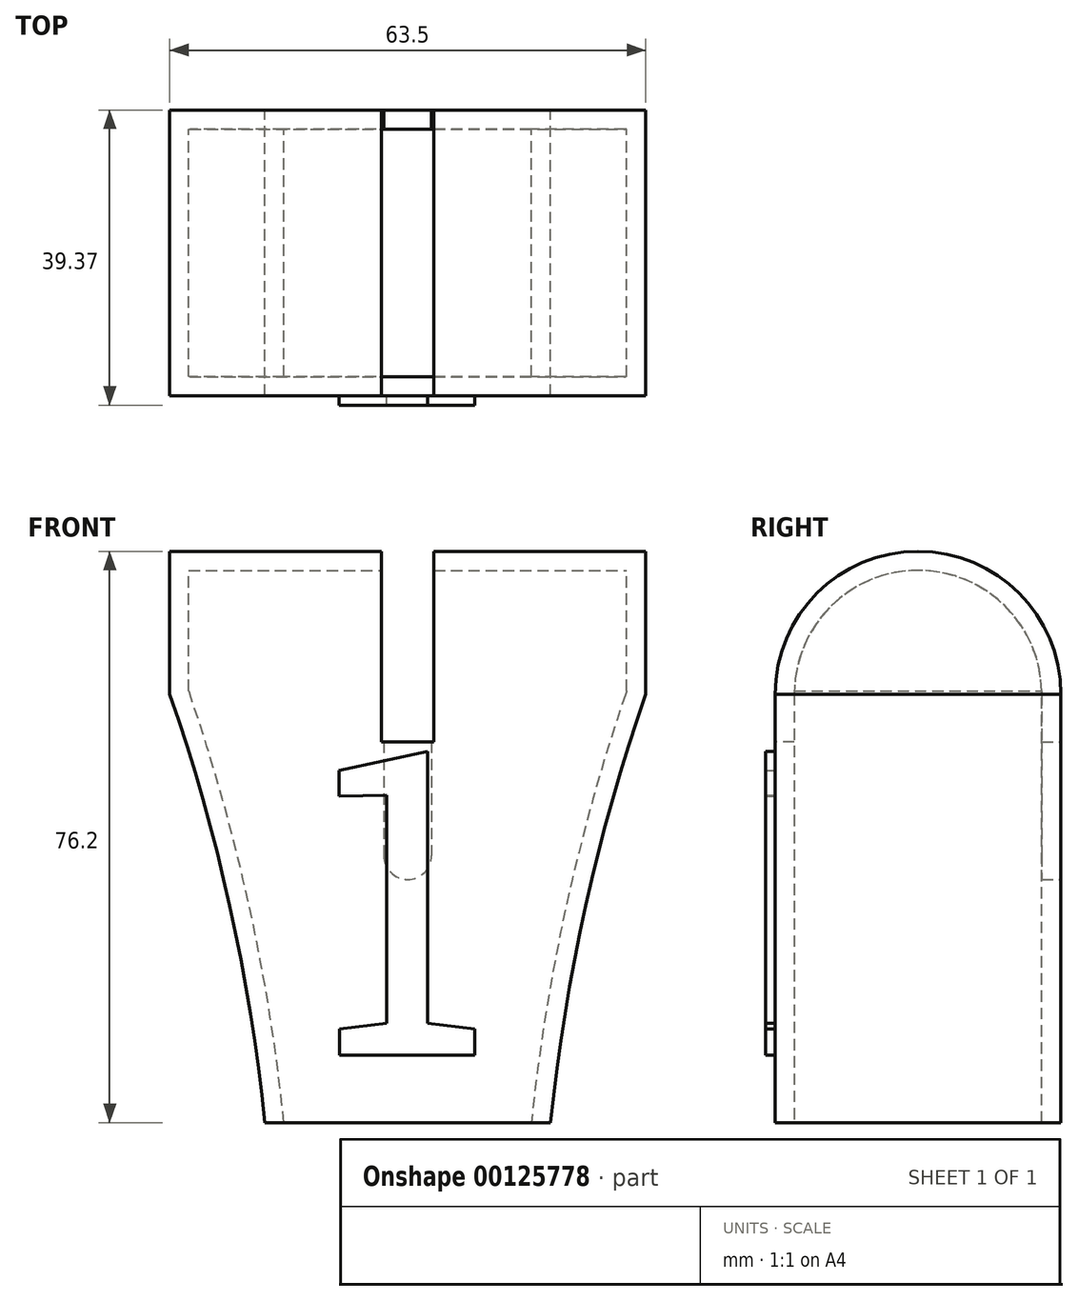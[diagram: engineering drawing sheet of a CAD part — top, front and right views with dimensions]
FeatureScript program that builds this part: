
annotation { "Feature Type Name" : "Feature", "Feature Type Description" : "" }
export const myFeature = defineFeature(function(context is Context, id is Id, definition is map)
    precondition{}
    {
        {
            var Q0;
            Q0=qCreatedBy(makeId("Front.planeOp"),FACE);
            var sketch = newSketch(context, id + "F0", { "sketchPlane" : qUnion([Q0])});
            skLineSegment(sketch, "E0.bottom", {"start": v(19.05, -38.1) * mm, "end": v(-19.05, -38.1) * mm});
            skLineSegment(sketch, "E0.top", {"start": v(31.75, 38.1) * mm, "end": v(-31.75, 38.1) * mm});
            skLineSegment(sketch, "E0.left", {"start": v(31.75, 19.05) * mm, "end": v(31.75, 38.1) * mm});
            skLineSegment(sketch, "E0.right", {"start": v(-31.75, 19.05) * mm, "end": v(-31.75, 38.1) * mm});
            skPoint(sketch, "E0.middle", {"position": v(0, 0) * mm});
            skPoint(sketch, "E1", {"position": v(31.75, 19.05) * mm});
            skPoint(sketch, "E2", {"position": v(-31.75, 19.05) * mm});
            skArc(sketch, "E3", {"start": v(31.75, 19.05) * mm, "mid": v(23.75, -9.16) * mm, "end": v(19.05, -38.1) * mm});
            skArc(sketch, "E4", {"start": v(-19.05, -38.1) * mm, "mid": v(-23.75, -9.16) * mm, "end": v(-31.75, 19.05) * mm});
            skPoint(sketch, "E5.orphan", {"position": v(31.75, -38.1) * mm});
            skPoint(sketch, "E6.orphan", {"position": v(-31.75, -38.1) * mm});
            skSolve(sketch);
        }
        {
            var Q0;
            Q0=qSketchRegion(id+"F0",true);
            extrude(context, id + "F1", {"entities" : qUnion([Q0]), "endBound" : BoundingType.SYMMETRIC, "depth" : 38.1 * mm});
        }
        {
            var Q0;
            Q0=qCreatedBy(makeId("Right.planeOp"),FACE);
            var sketch = newSketch(context, id + "F2", { "sketchPlane" : qUnion([Q0])});
            skArc(sketch, "E7", {"start": v(19.05, 19.05) * mm, "mid": v(0, 38.1) * mm, "end": v(-19.05, 19.05) * mm});
            skLineSegment(sketch, "E8", {"start": v(19.05, 19.05) * mm, "end": v(44.45, 19.05) * mm});
            skLineSegment(sketch, "E9", {"start": v(-19.05, 19.05) * mm, "end": v(-44.45, 19.05) * mm});
            skLineSegment(sketch, "E10", {"start": v(-44.45, 19.05) * mm, "end": v(-44.45, 44.45) * mm});
            skLineSegment(sketch, "E11", {"start": v(-44.45, 44.45) * mm, "end": v(44.45, 44.45) * mm});
            skLineSegment(sketch, "E12", {"start": v(44.45, 44.45) * mm, "end": v(44.45, 19.05) * mm});
            skPoint(sketch, "E13", {"position": v(0, 38.1) * mm});
            skSolve(sketch);
        }
        {
            var Q0;
            Q0=qSketchRegion(id+"F2",true);
            extrude(context, id + "F3", {"entities" : qUnion([Q0]), "operationType" : NewBodyOperationType.REMOVE, "endBound" : BoundingType.SYMMETRIC, "oppositeDirection" : true, "depth" : 127 * mm});
        }
        {
            var Q0;
            Q0=makeQuery(id+"F1.opExtrude","CAP_FACE",FACE,{"disambiguationData":[OSD([sQuery(id+"F0.wireOp",EDGE,"E0.bottom"),sQuery(id+"F0.wireOp",EDGE,"E0.top"),sQuery(id+"F0.wireOp",EDGE,"E0.left"),sQuery(id+"F0.wireOp",EDGE,"E0.right"),sQuery(id+"F0.wireOp",EDGE,"E3"),sQuery(id+"F0.wireOp",EDGE,"E4")])],"isStart":true});
            var sketch = newSketch(context, id + "F4", { "sketchPlane" : qUnion([Q0])});
            skLineSegment(sketch, "E14.bottom", {"start": v(3.17, -2.5) * mm, "end": v(-3.18, -2.5) * mm});
            skLineSegment(sketch, "E14.top", {"start": v(3.17, 29.26) * mm, "end": v(-3.18, 29.26) * mm});
            skLineSegment(sketch, "E14.left", {"start": v(3.17, -2.5) * mm, "end": v(3.17, 29.26) * mm});
            skLineSegment(sketch, "E14.right", {"start": v(-3.18, -2.5) * mm, "end": v(-3.18, 29.26) * mm});
            skPoint(sketch, "E14.middle", {"position": v(0, 13.38) * mm});
            skArc(sketch, "E15", {"start": v(3.17, 29.26) * mm, "mid": v(0, 32.43) * mm, "end": v(-3.18, 29.26) * mm});
            skLineSegment(sketch, "E16", {"start": v(-3.18, 13.38) * mm, "end": v(3.17, 13.38) * mm, "construction": true});
            skArc(sketch, "E17.MirrorCS", {"start": v(3.17, -2.5) * mm, "mid": v(0, -5.67) * mm, "end": v(-3.18, -2.5) * mm});
            skSolve(sketch);
        }
        {
            var Q0;
            Q0=makeQuery(id+"F1.opExtrude","SWEPT_FACE",FACE,{"disambiguationData":[OSD([sQuery(id+"F0.wireOp",EDGE,"E0.bottom")])]});
            shell(context, id + "F5", {"entities" : qUnion([Q0]), "thickness" : 2.54 * mm});
        }
        {
            var Q0;
            Q0=qSketchRegion(id+"F4",true);
            extrude(context, id + "F6", {"entities" : qUnion([Q0]), "operationType" : NewBodyOperationType.REMOVE, "oppositeDirection" : true, "depth" : 4.48 * mm});
        }
        {
            var Q0;
            Q0=qCreatedBy(makeId("Top.planeOp"),FACE);
            var Q1;
            Q1=sQuery(id+"F2.wireOp",VERTEX,"E13");
            cPlane(context, id + "F7", {"entities" : qUnion([Q0, Q1]), "cplaneType" : CPlaneType.PLANE_POINT, "offset" : 25.4 * mm, "width" : 152.4 * mm, "height" : 152.4 * mm});
        }
        {
            var Q0;
            Q0=qCreatedBy(id+"F7.planeOp",FACE);
            var sketch = newSketch(context, id + "F8", { "sketchPlane" : qUnion([Q0])});
            skLineSegment(sketch, "E18.bottom", {"start": v(-3.5, 19.05) * mm, "end": v(3.5, 19.05) * mm});
            skLineSegment(sketch, "E18.left", {"start": v(-3.5, 19.05) * mm, "end": v(-3.5, -19.05) * mm});
            skLineSegment(sketch, "E18.right", {"start": v(3.5, 19.05) * mm, "end": v(3.5, -19.05) * mm});
            skPoint(sketch, "E19", {"position": v(0, 0) * mm});
            skLineSegment(sketch, "E20", {"start": v(3.5, 0) * mm, "end": v(-3.5, 0) * mm, "construction": true});
            skLineSegment(sketch, "E21", {"start": v(-3.5, -19.05) * mm, "end": v(3.5, -19.05) * mm});
            skSolve(sketch);
        }
        {
            var Q0;
            Q0=qSketchRegion(id+"F8",true);
            extrude(context, id + "F9", {"entities" : qUnion([Q0]), "operationType" : NewBodyOperationType.REMOVE, "oppositeDirection" : true, "depth" : 25.4 * mm});
        }
        {
            var Q0;
            Q0=makeQuery(id+"F1.opExtrude","CAP_FACE",FACE,{"disambiguationData":[OSD([sQuery(id+"F0.wireOp",EDGE,"E0.bottom"),sQuery(id+"F0.wireOp",EDGE,"E0.top"),sQuery(id+"F0.wireOp",EDGE,"E0.left"),sQuery(id+"F0.wireOp",EDGE,"E0.right"),sQuery(id+"F0.wireOp",EDGE,"E3"),sQuery(id+"F0.wireOp",EDGE,"E4")])],"isStart":false});
            var sketch = newSketch(context, id + "F10", { "sketchPlane" : qUnion([Q0])});
            skText(sketch, "E22", { "text": "1", "fontName": "RobotoSlab-Regular.ttf"});
            const initialGuessF10  = {"E22": [-0.01245, -0.02912, 1, 0, 0.04107]};
            skSetInitialGuess(sketch, initialGuessF10);
            skSolve(sketch);
        }
        {
            var Q0;
            Q0=qSketchRegion(id+"F10",true);
            extrude(context, id + "F11", {"entities" : qUnion([Q0]), "operationType" : NewBodyOperationType.ADD, "depth" : 1.27 * mm});
        }
    });
